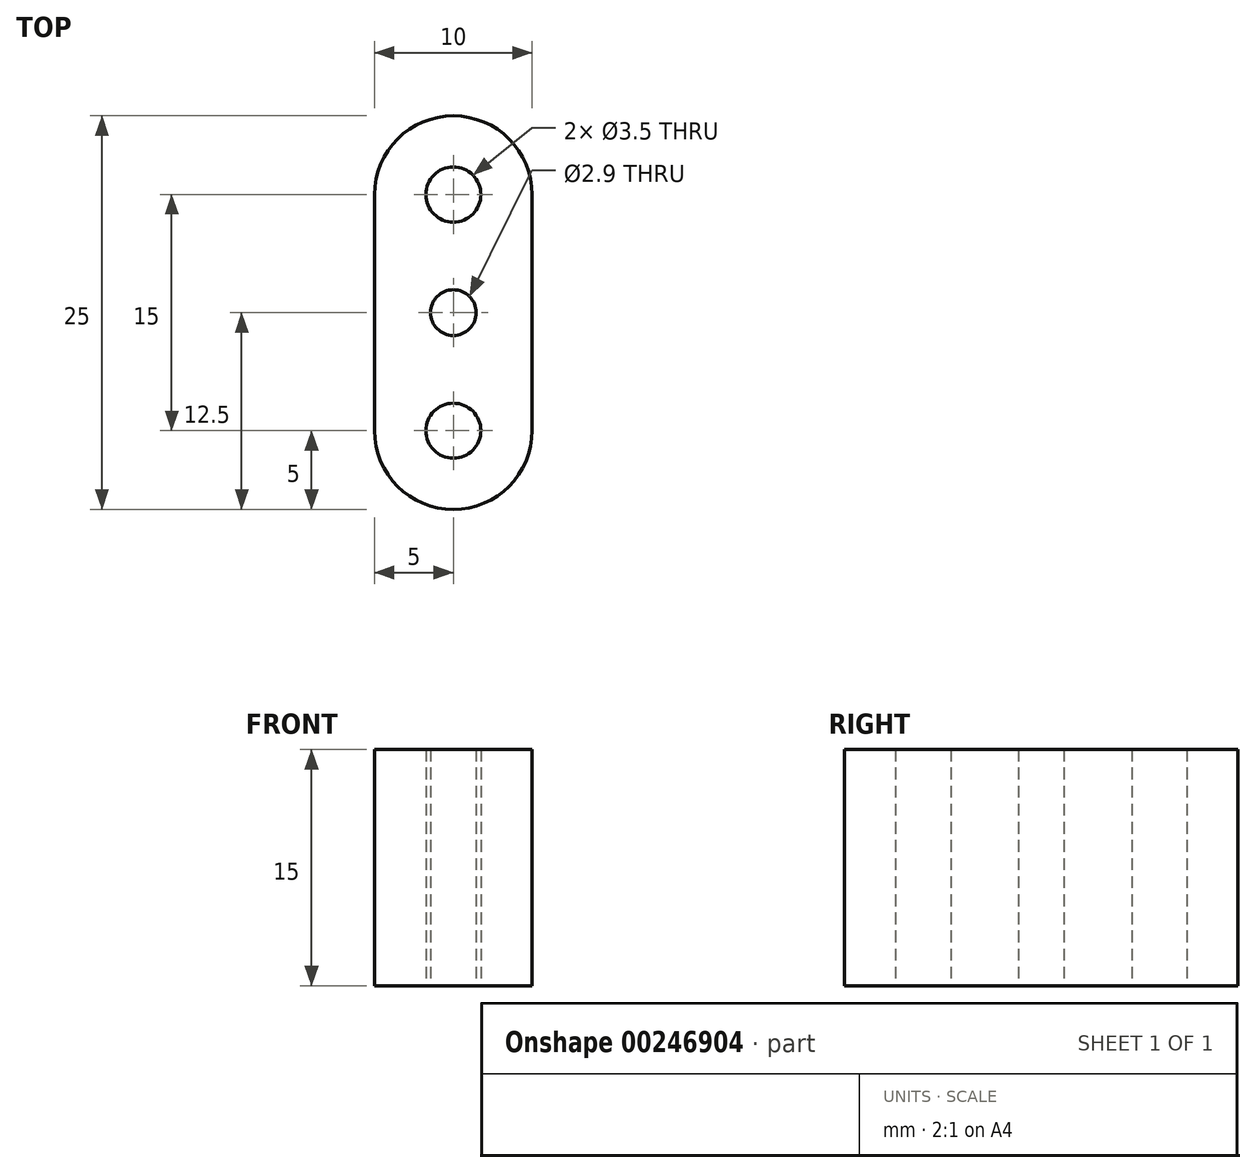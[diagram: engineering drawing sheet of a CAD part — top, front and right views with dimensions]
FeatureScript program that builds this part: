
annotation { "Feature Type Name" : "Feature", "Feature Type Description" : "" }
export const myFeature = defineFeature(function(context is Context, id is Id, definition is map)
    precondition{}
    {
        {
            var Q0;
            Q0=qCreatedBy(makeId("Top.planeOp"),FACE);
            var sketch = newSketch(context, id + "F0", { "sketchPlane" : qUnion([Q0])});
            skLineSegment(sketch, "E0.bottom", {"start": v(5, -12.5) * mm, "end": v(-5, -12.5) * mm});
            skLineSegment(sketch, "E0.top", {"start": v(5, 12.5) * mm, "end": v(-5, 12.5) * mm});
            skLineSegment(sketch, "E0.left", {"start": v(5, -12.5) * mm, "end": v(5, 12.5) * mm});
            skLineSegment(sketch, "E0.right", {"start": v(-5, -12.5) * mm, "end": v(-5, 12.5) * mm});
            skPoint(sketch, "E0.middle", {"position": v(0, 0) * mm});
            skCircle(sketch, "E1", {"center": v(0, 0) * mm, "radius": 1.45 * mm});
            skCircle(sketch, "E2", {"center": v(0, -7.5) * mm, "radius": 1.75 * mm});
            skCircle(sketch, "E3.MirrorC", {"center": v(0, 7.5) * mm, "radius": 1.75 * mm});
            skSolve(sketch);
        }
        {
            var Q0;
            Q0 = qSketchRegion(id + "F0", true);
            extrude(context, id + "F1", {"entities" : qUnion([Q0]), "depth" : 15 * mm});
        }
        {
            var Q0;
            Q0=makeQuery(id+"F1.opExtrude","SWEPT_EDGE",EDGE,{"disambiguationData":[OSD([sQuery(id+"F0.wireOp",EDGE,"E0.bottom"),sQuery(id+"F0.wireOp",EDGE,"E0.right")])]});
            var Q1;
            Q1=makeQuery(id+"F1.opExtrude","SWEPT_EDGE",EDGE,{"disambiguationData":[OSD([sQuery(id+"F0.wireOp",EDGE,"E0.bottom"),sQuery(id+"F0.wireOp",EDGE,"E0.left")])]});
            var Q2;
            Q2=makeQuery(id+"F1.opExtrude","SWEPT_EDGE",EDGE,{"disambiguationData":[OSD([sQuery(id+"F0.wireOp",EDGE,"E0.top"),sQuery(id+"F0.wireOp",EDGE,"E0.right")])]});
            var Q3;
            Q3=makeQuery(id+"F1.opExtrude","SWEPT_EDGE",EDGE,{"disambiguationData":[OSD([sQuery(id+"F0.wireOp",EDGE,"E0.top"),sQuery(id+"F0.wireOp",EDGE,"E0.left")])]});
            fillet(context, id + "F2", {"entities" : qUnion([Q0, Q1, Q2, Q3]), "radius" : 5 * mm, "tangentPropagation" : true, "allowEdgeOverflow" : false});
        }
    });
